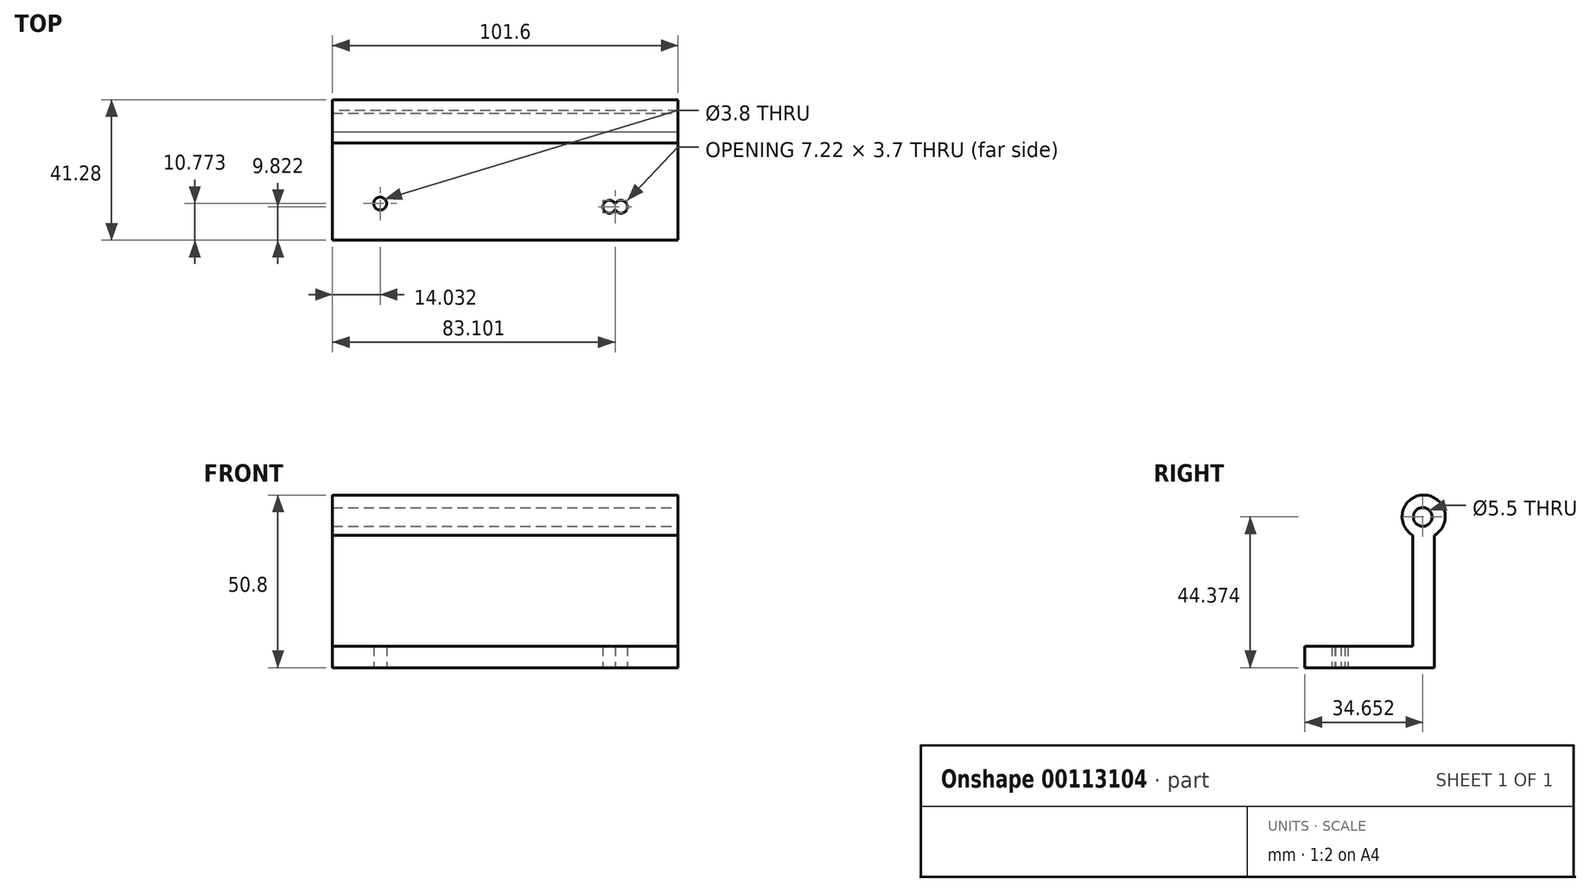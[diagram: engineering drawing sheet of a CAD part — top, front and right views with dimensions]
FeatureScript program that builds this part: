
annotation { "Feature Type Name" : "Feature", "Feature Type Description" : "" }
export const myFeature = defineFeature(function(context is Context, id is Id, definition is map)
    precondition{}
    {
        {
            var Q0;
            Q0=qCreatedBy(makeId("Right.planeOp"),FACE);
            var sketch = newSketch(context, id + "F0", { "sketchPlane" : qUnion([Q0])});
            skLineSegment(sketch, "E0.bottom", {"start": v(19.05, -3.18) * mm, "end": v(-19.05, -3.18) * mm});
            skLineSegment(sketch, "E0.top", {"start": v(19.05, 3.17) * mm, "end": v(-19.05, 3.17) * mm});
            skLineSegment(sketch, "E0.left", {"start": v(19.05, -3.18) * mm, "end": v(19.05, 3.17) * mm});
            skLineSegment(sketch, "E0.right", {"start": v(-19.05, -3.18) * mm, "end": v(-19.05, 3.17) * mm});
            skPoint(sketch, "E0.middle", {"position": v(0, 0) * mm});
            skLineSegment(sketch, "E1.bottom", {"start": v(12.7, 41.27) * mm, "end": v(19.05, 41.27) * mm});
            skLineSegment(sketch, "E1.top", {"start": v(12.7, 3.17) * mm, "end": v(19.05, 3.17) * mm});
            skLineSegment(sketch, "E1.left", {"start": v(12.7, 41.27) * mm, "end": v(12.7, 3.17) * mm});
            skLineSegment(sketch, "E1.right", {"start": v(19.05, 41.27) * mm, "end": v(19.05, 3.17) * mm});
            skCircle(sketch, "E2", {"center": v(15.88, 41.27) * mm, "radius": 6.35 * mm});
            skSolve(sketch);
        }
        {
            var Q0;
            Q0 = qSketchRegion(id + "F0", true);
            extrude(context, id + "F1", {"entities" : qUnion([Q0]), "depth" : 101.6 * mm});
        }
        {
            var Q0;
            Q0=qCreatedBy(makeId("Right.planeOp"),FACE);
            var sketch = newSketch(context, id + "F2", { "sketchPlane" : qUnion([Q0])});
            skPoint(sketch, "E3", {"position": v(15.6, 41.2) * mm});
            skSolve(sketch);
        }
        {
            var Q0;
            Q0=sQuery(id+"F2.wireOp",VERTEX,"E3");
            var Q1;
            Q1=makeQuery(id+"F1.opExtrude","SWEPT_BODY",BODY,{"disambiguationData":[OSD([sQuery(id+"F0.wireOp",EDGE,"E0.bottom"),sQuery(id+"F0.wireOp",EDGE,"E0.top"),sQuery(id+"F0.wireOp",EDGE,"E0.left"),sQuery(id+"F0.wireOp",EDGE,"E0.right"),sQuery(id+"F0.wireOp",EDGE,"E1.left"),sQuery(id+"F0.wireOp",EDGE,"E1.right"),sQuery(id+"F0.wireOp",EDGE,"E2")])]});
            hole(context, id + "F3", {"style" : HoleStyle.SIMPLE, "endStyle" : HoleEndStyle.THROUGH, "oppositeDirection" : true, "holeDiameter" : 5.5 * mm, "locations" : qUnion([Q0]), "scope" : qUnion([Q1]), "isTappedThrough" : true, "startStyle" : HoleStartStyle.PART});
        }
        {
            var Q0;
            Q0=makeQuery(id+"F1.opExtrude","SWEPT_FACE",FACE,{"disambiguationData":[OSD([sQuery(id+"F0.wireOp",EDGE,"E0.top")])]});
            var sketch = newSketch(context, id + "F4", { "sketchPlane" : qUnion([Q0])});
            skPoint(sketch, "E4", {"position": v(14.03, -8.28) * mm});
            skPoint(sketch, "E5", {"position": v(81.39, -9.23) * mm});
            skPoint(sketch, "E6", {"position": v(84.81, -9.23) * mm});
            skSolve(sketch);
        }
        {
            var Q0;
            Q0=sQuery(id+"F4.wireOp",VERTEX,"E4");
            var Q1;
            Q1=sQuery(id+"F4.wireOp",VERTEX,"E5");
            var Q2;
            Q2=sQuery(id+"F4.wireOp",VERTEX,"E6");
            var Q3;
            Q3=makeQuery(id+"F1.opExtrude","SWEPT_BODY",BODY,{"disambiguationData":[OSD([sQuery(id+"F0.wireOp",EDGE,"E0.bottom"),sQuery(id+"F0.wireOp",EDGE,"E0.top"),sQuery(id+"F0.wireOp",EDGE,"E0.left"),sQuery(id+"F0.wireOp",EDGE,"E0.right"),sQuery(id+"F0.wireOp",EDGE,"E1.left"),sQuery(id+"F0.wireOp",EDGE,"E1.right"),sQuery(id+"F0.wireOp",EDGE,"E2")])]});
            hole(context, id + "F5", {"style" : HoleStyle.SIMPLE, "endStyle" : HoleEndStyle.THROUGH, "standardTappedOrClearance" : lookupTablePath({ "standard" : "ANSI", "fit" : "Normal (ASME)", "size" : "#6", "type" : "Clearance" }), "standardBlindInLast" : lookupTablePath({ "fit" : "Free", "standard" : "ANSI", "size" : "#6", "type" : "Clearance" }), "holeDiameter" : 3.8 * mm, "locations" : qUnion([Q0, Q1, Q2]), "scope" : qUnion([Q3]), "isTappedThrough" : true, "startStyle" : HoleStartStyle.PART});
        }
    });
